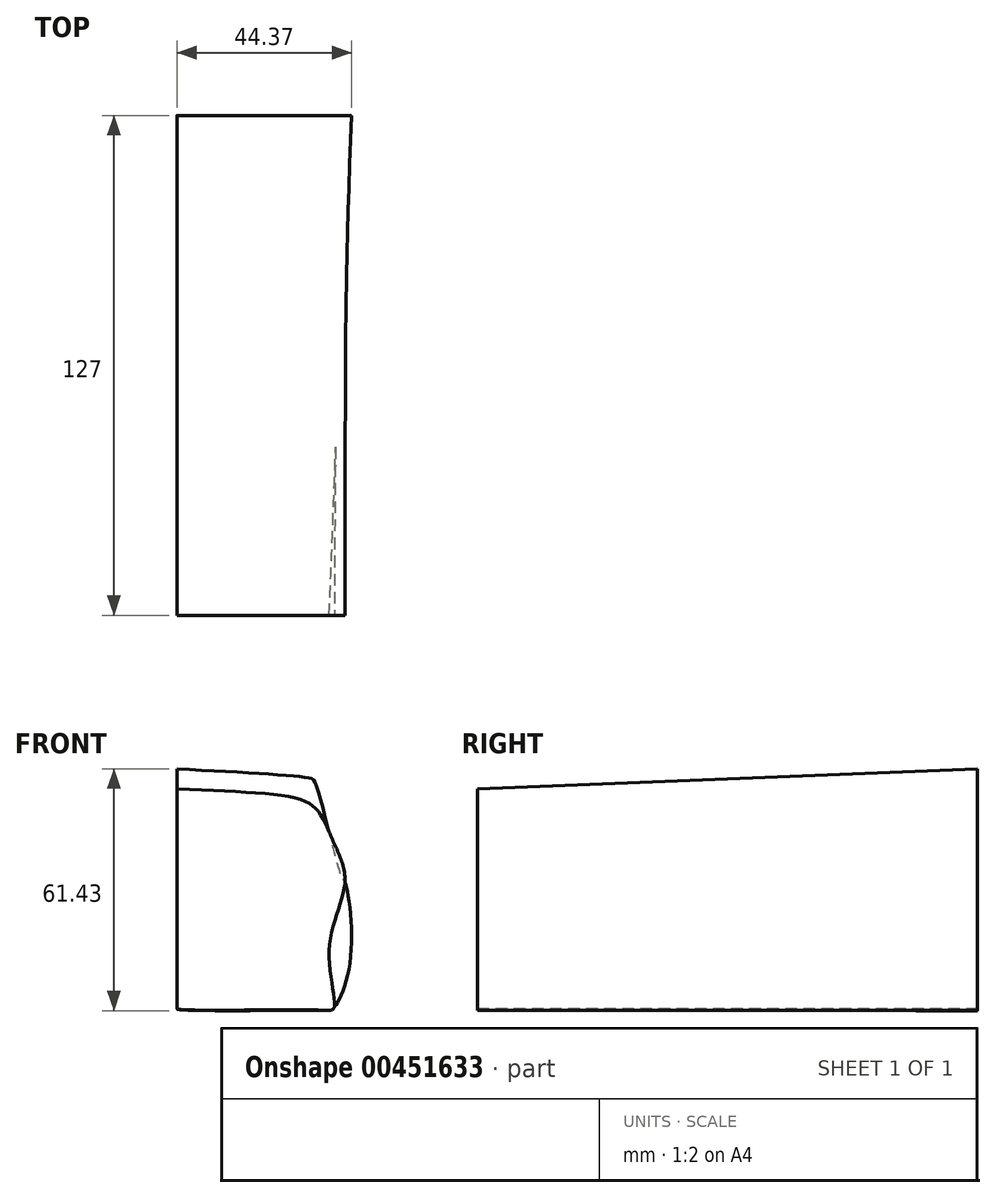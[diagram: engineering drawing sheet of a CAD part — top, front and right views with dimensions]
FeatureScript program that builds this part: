
annotation { "Feature Type Name" : "Feature", "Feature Type Description" : "" }
export const myFeature = defineFeature(function(context is Context, id is Id, definition is map)
    precondition{}
    {
        {
            var Q0;
            Q0=qCreatedBy(makeId("Front.planeOp"),FACE);
            var sketch = newSketch(context, id + "F0", { "sketchPlane" : qUnion([Q0])});
            skFitSpline(sketch, "E0", {"points": [v(0, 64.84) * mm, v(33.22, 62.6) * mm, v(35.45, 60.53) * mm, v(41.84, 37.21) * mm, v(42.64, 36.1) * mm, v(44.08, 16.77) * mm, v(39.93, 4.31) * mm, v(35.93, 3.51) * mm, v(0, 3.83) * mm, v(0, 4) * mm], "startDerivative": vector(226.02, -11.78) * mm, "endDerivative": vector(8.58, 12.4) * mm});
            skLineSegment(sketch, "E1", {"start": v(0, 64.84) * mm, "end": v(0, 4) * mm});
            skSolve(sketch);
        }
        {
            var Q0;
            Q0=qCreatedBy(makeId("Front.planeOp"),FACE);
            cPlane(context, id + "F1", {"entities" : qUnion([Q0]), "cplaneType" : CPlaneType.OFFSET, "offset" : 127 * mm, "width" : 152.4 * mm, "height" : 152.4 * mm});
        }
        {
            var Q0;
            Q0=qCreatedBy(id+"F1.planeOp",FACE);
            var sketch = newSketch(context, id + "F2", { "sketchPlane" : qUnion([Q0])});
            skFitSpline(sketch, "E2", {"points": [v(0, 59.75) * mm, v(31.23, 57.1) * mm, v(36.31, 53.45) * mm, v(39.8, 46.21) * mm, v(42.68, 36.15) * mm, v(38.71, 19.43) * mm, v(39.96, 4.37) * mm, v(35.97, 3.57) * mm, v(0.04, 3.89) * mm, v(0.04, 4.05) * mm], "startDerivative": vector(226.02, -11.78) * mm, "endDerivative": vector(8.58, 12.4) * mm});
            skLineSegment(sketch, "E3", {"start": v(0, 59.75) * mm, "end": v(0.04, 4.05) * mm});
            skSolve(sketch);
        }
        {
            var Q0;
            Q0 = qSketchRegion(id + "F2", true);
            var Q1;
            Q1 = qSketchRegion(id + "F0", true);
            loft(context, id + "F3", {"sheetProfilesArray" : [{ "sheetProfileEntities" : qUnion([Q0]) }, { "sheetProfileEntities" : qUnion([Q1]) }]});
        }
    });
